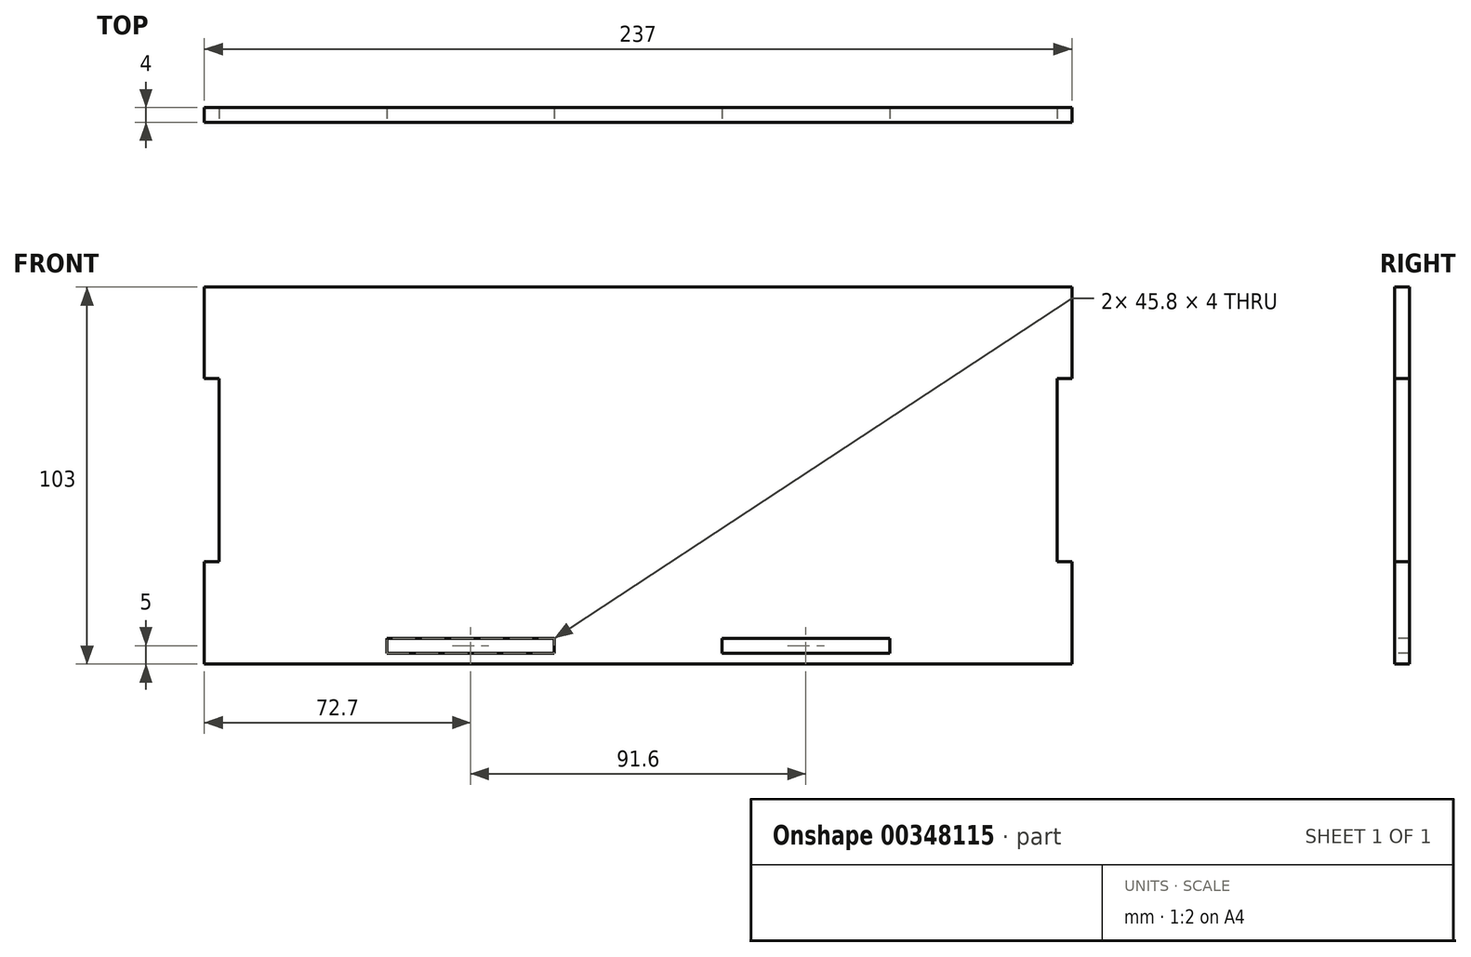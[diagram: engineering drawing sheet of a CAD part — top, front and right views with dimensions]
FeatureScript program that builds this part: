
annotation { "Feature Type Name" : "Feature", "Feature Type Description" : "" }
export const myFeature = defineFeature(function(context is Context, id is Id, definition is map)
    precondition{}
    {
        {
            var Q0;
            Q0=qCreatedBy(makeId("Front.planeOp"),FACE);
            var sketch = newSketch(context, id + "F0", { "sketchPlane" : qUnion([Q0])});
            skLineSegment(sketch, "E0.bottom", {"start": v(0, 0) * mm, "end": v(237, 0) * mm});
            skLineSegment(sketch, "E0.top", {"start": v(0, 103) * mm, "end": v(237, 103) * mm});
            skLineSegment(sketch, "E0.left", {"start": v(0, 0) * mm, "end": v(0, 103) * mm});
            skLineSegment(sketch, "E0.right", {"start": v(237, 0) * mm, "end": v(237, 103) * mm});
            skSolve(sketch);
        }
        {
            var Q0;
            Q0 = qSketchRegion(id + "F0", true);
            extrude(context, id + "F1", {"entities" : qUnion([Q0]), "depth" : 4 * mm});
        }
        {
            var Q0;
            Q0=makeQuery(id+"F1.opExtrude","CAP_FACE",FACE,{"disambiguationData":[OSD([sQuery(id+"F0.wireOp",EDGE,"E0.bottom"),sQuery(id+"F0.wireOp",EDGE,"E0.top"),sQuery(id+"F0.wireOp",EDGE,"E0.left"),sQuery(id+"F0.wireOp",EDGE,"E0.right")])],"isStart":false});
            var sketch = newSketch(context, id + "F2", { "sketchPlane" : qUnion([Q0])});
            skLineSegment(sketch, "E1", {"start": v(0, 3) * mm, "end": v(237, 3) * mm, "construction": true});
            skLineSegment(sketch, "E2.bottom", {"start": v(49.8, 3) * mm, "end": v(95.6, 3) * mm});
            skLineSegment(sketch, "E2.top", {"start": v(49.8, 7) * mm, "end": v(95.6, 7) * mm});
            skLineSegment(sketch, "E2.left", {"start": v(49.8, 3) * mm, "end": v(49.8, 7) * mm});
            skLineSegment(sketch, "E2.right", {"start": v(95.6, 3) * mm, "end": v(95.6, 7) * mm});
            skLineSegment(sketch, "E3.bottom", {"start": v(141.4, 3) * mm, "end": v(187.2, 3) * mm});
            skLineSegment(sketch, "E3.top", {"start": v(141.4, 7) * mm, "end": v(187.2, 7) * mm});
            skLineSegment(sketch, "E3.left", {"start": v(141.4, 3) * mm, "end": v(141.4, 7) * mm});
            skLineSegment(sketch, "E3.right", {"start": v(187.2, 3) * mm, "end": v(187.2, 7) * mm});
            skLineSegment(sketch, "E4", {"start": v(118.5, 103) * mm, "end": v(118.5, 3) * mm, "construction": true});
            skLineSegment(sketch, "E5.bottom", {"start": v(0, 78) * mm, "end": v(4, 78) * mm});
            skLineSegment(sketch, "E5.top", {"start": v(0, 28) * mm, "end": v(4, 28) * mm});
            skLineSegment(sketch, "E5.left", {"start": v(0, 78) * mm, "end": v(0, 28) * mm});
            skLineSegment(sketch, "E5.right", {"start": v(4, 78) * mm, "end": v(4, 28) * mm});
            skLineSegment(sketch, "E6.MirrorCS", {"start": v(237, 78) * mm, "end": v(233, 78) * mm});
            skLineSegment(sketch, "E7.MirrorCS", {"start": v(237, 28) * mm, "end": v(233, 28) * mm});
            skLineSegment(sketch, "E8.MirrorCS", {"start": v(233, 78) * mm, "end": v(233, 28) * mm});
            skLineSegment(sketch, "E9.MirrorCS", {"start": v(237, 78) * mm, "end": v(237, 28) * mm});
            skLineSegment(sketch, "E10", {"start": v(95.6, 7) * mm, "end": v(141.4, 7) * mm, "construction": true});
            skSolve(sketch);
        }
        {
            var Q0;
            Q0 = qSketchRegion(id + "F2", true);
            extrude(context, id + "F3", {"entities" : qUnion([Q0]), "operationType" : NewBodyOperationType.REMOVE, "endBound" : BoundingType.UP_TO_NEXT, "oppositeDirection" : true, "depth" : 25 * mm});
        }
    });
